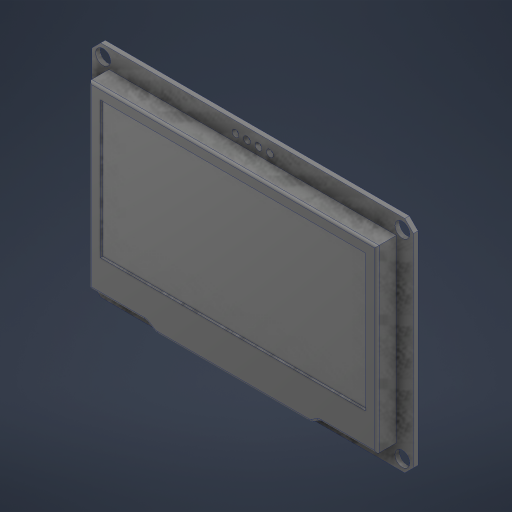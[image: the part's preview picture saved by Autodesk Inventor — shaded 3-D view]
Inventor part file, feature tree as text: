
AUTODESK INVENTOR PART (.ipt)
format: ipt  version: 2024 (Build 280153000, 153)  size: 326,144 bytes
history: native  units: mm
features: other x5, extrude x2, sketch x2, chamfer x1
ambient origin geometry x8: Origin, YZ Plane, XZ Plane, XY Plane, X Axis, Y Axis, Z Axis, Center Point
bodies: Body1 (feature_tree), Body2 (feature_tree)
feature tree (10):
  other  "Sólido1"
  other  "Edición directa1"
  extrude  "Extrusión1"  Depth=10.0mm
  extrude  "Extrusión2"  Depth=20.0mm
  other  "Sólido2"
  sketch  "Boceto1"  dims[d0=107.6mm d1=10.0mm d2=10.0mm d3=30.0mm]
  sketch  "Boceto2"  dims[d4=40.0mm d5=0.0mm d7=20.0mm d8=20.0mm d9=0.0mm]
  other  "Barrer1"
  chamfer  "Chaflán1"  Distance=20.0mm
  other  "Escala1"
